# Revit family: H-900
name_source: partatom
category: Plumbing Fixtures
revit_build: Autodesk Revit 2014 (Build: 20130308_1515(x64)
units: mm (PartAtom-declared; Revit-internal decimal feet)

## types (1)
- H-900
    CW Connection = Yes
    Chrome = Brass Chromed
    Compliance = NOM-008-CONAGUA-1998
    Description = Fixed Stream Nuva Showerhead and Arm
    Documentation = http://www.helvex.com.mx
    Features = Low, Medium and High Pressure Showerhead; Dynamic Water Economizer Included
    Fitting = ½" - 14 Npt
    HW Connection = Yes
    Instructive = http://www.helvex.com.mx
    Manufacturer = Helvex
    Max. Water Flow = 2.6 gal/min
    Max. Working Pressure = 85.3 psi
    Min. Water Flow = 1.1 gal/min
    Min. Working Pressure = 2.9 psi
    Model = H-900
    Niquel Duravex = Niquel Duravex
    Satin = Brass Satin
    Support Base Diameter = 2"
    Type Comments = Showerheads
    URL = http://www.helvex.com.mx

## geometry (parser evidence)
native form markers: Sweep x1
no freeform markers — native parametric forms only
